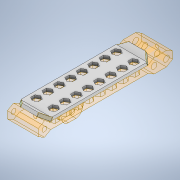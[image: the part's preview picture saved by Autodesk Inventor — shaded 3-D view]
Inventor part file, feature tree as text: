
AUTODESK INVENTOR PART (.ipt)
format: ipt  version: 2020 (Build 240168000, 168)  size: 474,624 bytes
history: native  units: in
note: dims shown in document units (in); Inventor stores cm internally (conversion verified against a paired STEP export)
features: extrude x7, sketch x7, other x4, plane x4
ambient origin geometry x8: Origin, YZ Plane, XZ Plane, XY Plane, X Axis, Y Axis, Z Axis, Center Point
bodies: Solid1 (feature_tree)
feature tree (22):
  other  "HexFlipper.ipt"
  extrude  "Extrusion1"  Depth=0.0787in TaperAngle=0.0deg
  extrude  "Extrusion2"  Depth=0.0787in TaperAngle=0.0deg
  extrude  "Extrusion3"  TaperAngle=135.0deg  [1 undecoded]
  plane  "Work Plane1"
  extrude  "Extrusion4"  Depth=0.9518in TaperAngle=0.0deg
  plane  "Work Plane2"
  extrude  "Extrusion5"  TaperAngle=135.0deg  [1 undecoded]
  plane  "Work Plane3"
  extrude  "Extrusion6"  TaperAngle=0.0deg  [1 undecoded]
  plane  "Work Plane4"
  extrude  "Extrusion7"  [1 undecoded]
  other  "TaggingFeature1"
  sketch  "Sketch1"  dims[d0=0.3937in d1=0.0787in d2=0.0in]
  sketch  "Sketch2"  dims[d3=0.0787in d4=0.0in d5=0.0787in d6=0.0in]
  sketch  "Sketch3"  dims[d7=45.0deg d8=135.0deg]
  sketch  "Sketch4"  dims[d9=0.8199in d10=0.0in d11=0.9518in d12=0.0in]
  sketch  "Sketch5"  dims[d13=45.0deg d14=135.0deg]
  sketch  "Sketch6"  dims[d15=0.0in d16=0.0in d17=0.0in d18=0.0in]
  sketch  "Sketch7"
  other  "Solid1::HexFlipper.ipt"
  other  "Srf1"
note: 4 required parameter values undecoded (feature->parameter linkage not recoverable at this tier; creation-order binding heuristic only, values carry confidence <= 0.55)
